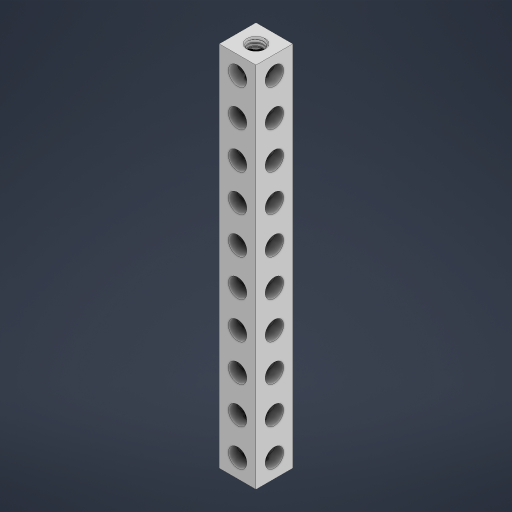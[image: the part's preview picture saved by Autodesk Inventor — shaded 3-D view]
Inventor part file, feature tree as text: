
AUTODESK INVENTOR PART (.ipt)
format: ipt  version: 2023 (Build 270158000, 158)  size: 1,391,104 bytes
history: native  units: in
note: dims shown in document units (in); Inventor stores cm internally (conversion verified against a paired STEP export)
features: mirror x1
ambient origin geometry x8: Origin, YZ Plane, XZ Plane, XY Plane, X Axis, Y Axis, Z Axis, Center Point
bodies: Solid1 (feature_tree)
feature tree (1):
  mirror  "Mirror3"
